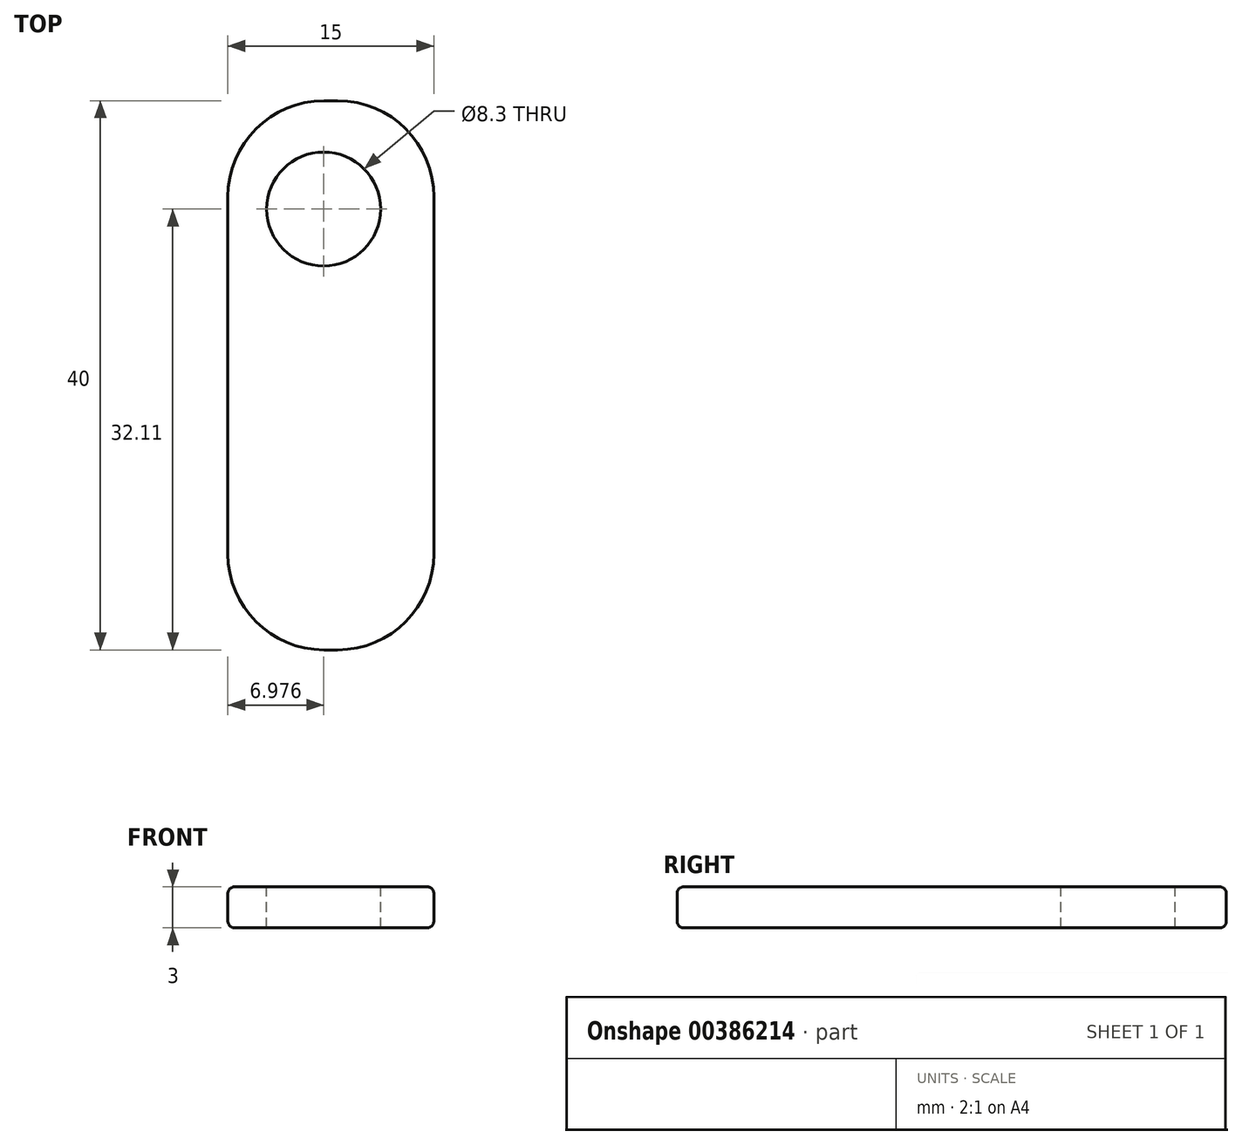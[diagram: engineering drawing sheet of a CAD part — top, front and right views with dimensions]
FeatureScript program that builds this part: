
annotation { "Feature Type Name" : "Feature", "Feature Type Description" : "" }
export const myFeature = defineFeature(function(context is Context, id is Id, definition is map)
    precondition{}
    {
        {
            var Q0;
            Q0=qCreatedBy(makeId("Top.planeOp"),FACE);
            var sketch = newSketch(context, id + "F0", { "sketchPlane" : qUnion([Q0])});
            skLineSegment(sketch, "E0.bottom", {"start": v(15, 0) * mm, "end": v(0, 0) * mm});
            skLineSegment(sketch, "E0.top", {"start": v(15, -40) * mm, "end": v(0, -40) * mm});
            skLineSegment(sketch, "E0.left", {"start": v(15, 0) * mm, "end": v(15, -40) * mm});
            skLineSegment(sketch, "E0.right", {"start": v(0, 0) * mm, "end": v(0, -40) * mm});
            skSolve(sketch);
        }
        {
            var Q0;
            Q0=makeQuery(id+"F0.imprint","IMPRINT",FACE,{"disambiguationData":[TD([[makeQuery(id+"F0.imprint","IMPRINT",EDGE,{"derivedFrom":sQuery(id+"F0.wireOp",EDGE,"E0.bottom")}),1.0]])]});
            extrude(context, id + "F1", {"entities" : qUnion([Q0]), "depth" : 3 * mm});
        }
        {
            var Q0;
            Q0=makeQuery(id+"F1.opExtrude","CAP_FACE",FACE,{"disambiguationData":[OSD([sQuery(id+"F0.wireOp",EDGE,"E0.bottom"),sQuery(id+"F0.wireOp",EDGE,"E0.top"),sQuery(id+"F0.wireOp",EDGE,"E0.left"),sQuery(id+"F0.wireOp",EDGE,"E0.right")])],"isStart":false});
            var Q1;
            Q1=makeQuery(id+"F1.opExtrude","CAP_FACE",FACE,{"disambiguationData":[OSD([sQuery(id+"F0.wireOp",EDGE,"E0.bottom"),sQuery(id+"F0.wireOp",EDGE,"E0.top"),sQuery(id+"F0.wireOp",EDGE,"E0.left"),sQuery(id+"F0.wireOp",EDGE,"E0.right")])],"isStart":true});
            fillet(context, id + "F2", {"entities" : qUnion([Q0, Q1]), "radius" : 0.5 * mm, "tangentPropagation" : true, "allowEdgeOverflow" : false});
        }
        {
            var Q0;
            Q0=makeQuery(id+"F1.opExtrude","SWEPT_EDGE",EDGE,{"disambiguationData":[OSD([sQuery(id+"F0.wireOp",EDGE,"E0.bottom"),sQuery(id+"F0.wireOp",EDGE,"E0.left")])]});
            var Q1;
            Q1=makeQuery(id+"F1.opExtrude","SWEPT_EDGE",EDGE,{"disambiguationData":[OSD([sQuery(id+"F0.wireOp",EDGE,"E0.bottom"),sQuery(id+"F0.wireOp",EDGE,"E0.right")])]});
            var Q2;
            Q2=makeQuery(id+"F1.opExtrude","SWEPT_EDGE",EDGE,{"disambiguationData":[OSD([sQuery(id+"F0.wireOp",EDGE,"E0.top"),sQuery(id+"F0.wireOp",EDGE,"E0.left")])]});
            var Q3;
            Q3=makeQuery(id+"F1.opExtrude","SWEPT_EDGE",EDGE,{"disambiguationData":[OSD([sQuery(id+"F0.wireOp",EDGE,"E0.top"),sQuery(id+"F0.wireOp",EDGE,"E0.right")])]});
            fillet(context, id + "F3", {"entities" : qUnion([Q0, Q1, Q2, Q3]), "radius" : 7 * mm, "tangentPropagation" : true, "allowEdgeOverflow" : false});
        }
        {
            var Q0;
            Q0=makeQuery(id+"F1.opExtrude","CAP_FACE",FACE,{"disambiguationData":[OSD([sQuery(id+"F0.wireOp",EDGE,"E0.bottom"),sQuery(id+"F0.wireOp",EDGE,"E0.top"),sQuery(id+"F0.wireOp",EDGE,"E0.left"),sQuery(id+"F0.wireOp",EDGE,"E0.right")])],"isStart":false});
            var sketch = newSketch(context, id + "F4", { "sketchPlane" : qUnion([Q0])});
            skCircle(sketch, "E1", {"center": v(6.98, -7.9) * mm, "radius": 4.15 * mm});
            skSolve(sketch);
        }
        {
            var Q0;
            Q0=makeQuery(id+"F4.imprint","IMPRINT",FACE,{"disambiguationData":[TD([[makeQuery(id+"F4.imprint","IMPRINT",EDGE,{"derivedFrom":sQuery(id+"F4.wireOp",EDGE,"E1")}),1.0]])]});
            extrude(context, id + "F5", {"entities" : qUnion([Q0]), "operationType" : NewBodyOperationType.REMOVE, "oppositeDirection" : true, "depth" : 25 * mm});
        }
    });
